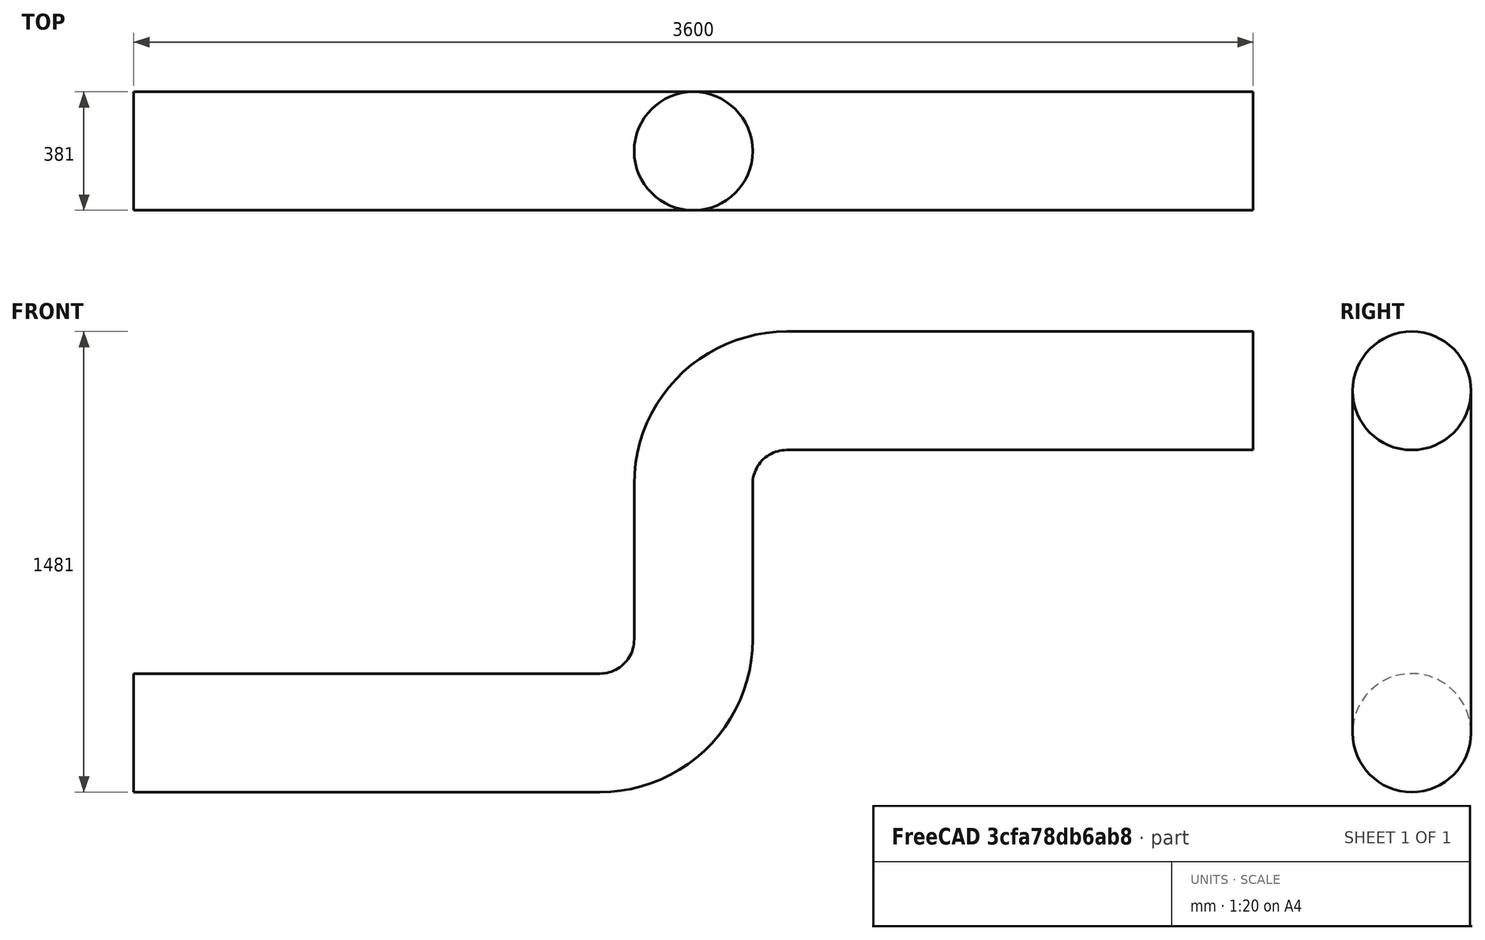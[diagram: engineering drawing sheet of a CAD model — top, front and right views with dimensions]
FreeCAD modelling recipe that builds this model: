
FCSTD DOCUMENT  (FreeCAD 0.21R33771 (Git))
Label: example_pipe
License: All rights reserved
LicenseURL: http://en.wikipedia.org/wiki/All_rights_reserved
objects: Part::FeaturePython×7, Sketcher::SketchObject×2, App::DocumentObjectGroupPython×2, PartDesign::AdditivePipe×1, PartDesign::Body×1, App::MaterialObjectPython×1, Fem::FemMeshObject×1
note: 12 computed .brp shape members not serialized (recipe doc carries the construction recipe); baked Part::Feature solids carry a one-line shape summary decoded from their .brp

FEATURE [Sketcher::SketchObject] Sketch
  FullyConstrained = true
  MapMode = 5
  Placement = pos=(0,0,0) rot=(0.57735,0.57735,0.57735;2.0944rad)
  Support = -> [YZ_Plane]
  sketch-geometry (1):
    g0: Circle CenterX=0 CenterY=0 CenterZ=0 NormalX=0 NormalY=0 NormalZ=1 AngleXU=0 Radius=190.5
  constraints (2):
    c: Coincident(g0,g-1)
    c: Diameter(g0) = 381
FEATURE [Sketcher::SketchObject] Sketch001
  FullyConstrained = false
  MapMode = 5
  Placement = pos=(0,0,0) rot=(1,0,0;1.5708rad)
  Support = -> [XZ_Plane]
  sketch-geometry (6):
    g0: LineSegment StartX=0 StartY=0 StartZ=0 EndX=1500 EndY=0 EndZ=0
    g1: LineSegment StartX=1800 StartY=300 StartZ=0 EndX=1800 EndY=800 EndZ=0
    g2: LineSegment StartX=2100 StartY=1100 StartZ=0 EndX=3600 EndY=1100 EndZ=0
    g3: ArcOfCircle CenterX=1500 CenterY=300 CenterZ=0 NormalX=0 NormalY=0 NormalZ=1 AngleXU=0 Radius=300 StartAngle=4.71239 EndAngle=6.28319
    g4: ArcOfCircle CenterX=1800 CenterY=800 CenterZ=0 NormalX=0 NormalY=0 NormalZ=1 AngleXU=0 Radius=1.41545e-06 StartAngle=1.5708 EndAngle=3.14159
    g5: ArcOfCircle CenterX=2100 CenterY=800 CenterZ=0 NormalX=0 NormalY=0 NormalZ=1 AngleXU=0 Radius=300 StartAngle=1.5708 EndAngle=3.14159
  constraints (13):
    c: Coincident(g-1,g0)
    c: Horizontal(g0)
    c: Vertical(g1)
    c: Horizontal(g2)
    c: Tangent(g0,g3) = -1.5708
    c: Tangent(g1,g3) = -1.5708
    c: DistanceX(g0,g0) = 1500
    c: Radius(g3) = 300
    c: Tangent(g1,g5) = 1.5708
    c: Tangent(g2,g5) = 1.5708
    c: Radius(g5) = 300
    c: DistanceY(g1,g1) = 500
    c: DistanceX(g2,g2) = 1500
FEATURE [PartDesign::AdditivePipe] AdditivePipe
  AuxilleryCurvelinear = true
  AuxillerySpineTangent = false
  Binormal = (0,0,0)
  Mode = 0
  Placement = pos=(0,0,0) rot=(0.57735,0.57735,0.57735;2.0944rad)
  Profile = -> Sketch
  Spine = -> Sketch001 [Edge1,Edge2,Edge3,Edge5,Edge6]
  SpineTangent = false
  Transformation = 0
  Transition = 0
FEATURE [PartDesign::Body] Body
  Group = -> [Sketch,Sketch001,AdditivePipe]
  Origin = -> Origin
  Tip = -> AdditivePipe
FEATURE [Part::FeaturePython] PhysicsModel  # WARN: FeaturePython — macro-defined, semantics opaque (R4)
  Flow = 0
  Phase = 0
  SRFModelAxis = (0,0,0)
  SRFModelCoR = (0,0,0)
  SRFModelEnabled = false
  SRFModelRPM = 0
  Time = 0
  Turbulence = 3
  TurbulenceModel = 0
  gx = 0
  gy = -9800
  gz = 0
FEATURE [App::MaterialObjectPython] FluidProperties  label="Water"  # material (typed FeaturePython)
  Category = 1
  Material = CardName=WaterIsothermal; Density=998 kg/m^3; Description=Standard distilled water properties at 20 Degrees Celsius and 1 atm; DynamicViscosity=1.003e-3 kg/m/s; Name=Water; Type=Isothermal
FEATURE [Part::FeaturePython] InitialiseFields  # WARN: FeaturePython — macro-defined, semantics opaque (R4)
  PotentialFlow = false
  PotentialFlowP = false
  Pressure = 0
  ReThetat = 1
  Temperature = 290
  UseInletTemperatureValue = false
  UseInletTurbulenceValues = false
  UseInletUValues = false
  UseOutletPValue = false
  Ux = 0
  Uy = 0
  Uz = 0
  epsilon = 50000000
  gammaInt = 1
  k = 860
  nuTilda = 55000000
  nut = 50000000
  omega = 2
FEATURE [Part::FeaturePython] CfdSolver  # WARN: FeaturePython — macro-defined, semantics opaque (R4)
  ConvergenceTol = 0.001
  EndTime = 1
  InputCaseName = case
  MaxCFLNumber = 5
  MaxInterfaceCFLNumber = 5
  MaxIterations = 2000
  Parallel = true
  ParallelCores = 4
  PurgeWrite = 0
  StartFrom = 0
  SteadyWriteInterval = 100
  TimeStep = 0.001
  TransientWriteInterval = 0.1
FEATURE [Part::FeaturePython] CfdFluidBoundary  label="inlet"  # WARN: FeaturePython — macro-defined, semantics opaque (R4)
  BoundarySubType = 5
  BoundaryType = 1
  DefaultBoundary = false
  DissipationRate = 50000000
  HeatFlux = 0
  HeatTransferCoeff = 0
  Intermittency = 1
  MassFlowRate = 0
  NuTilda = 55000000
  PeriodicCentreOfRotation = (0,0,0)
  PeriodicCentreOfRotationAxis = (0,0,0)
  PeriodicMaster = true
  PeriodicSeparationVector = (0,0,0)
  PorousBaffleMethod = 0
  Pressure = 100
  PressureDropCoeff = 0
  ReThetat = 1
  RelativeToFrame = false
  ReverseNormal = false
  RotationalPeriodic = false
  RoughnessConstant = 0.5
  RoughnessHeight = 0
  ScreenSpacing = 2
  ScreenWireDiameter = 0.2
  ShapeRefs = -> [AdditivePipe]
  SlipRatio = 0
  SpecificDissipationRate = 1
  Temperature = 290
  ThermalBoundaryType = 0
  TurbulenceInletSpecification = 0
  TurbulenceIntensityPercentage = 0.02
  TurbulenceLengthScale = 14
  TurbulentKineticEnergy = 10000
  TurbulentViscosity = 50000000
  Ux = 1000
  Uy = 0
  Uz = 0
  VelocityIsCartesian = true
  VelocityMag = 0
  VolFlowRate = 0
  kEqnTurbulentKineticEnergy = 10000
  kEqnTurbulentViscosity = 50000000
FEATURE [Part::FeaturePython] CfdFluidBoundary001  label="outlet"  # WARN: FeaturePython — macro-defined, semantics opaque (R4)
  BoundarySubType = 10
  BoundaryType = 2
  DefaultBoundary = false
  DissipationRate = 50000000
  HeatFlux = 0
  HeatTransferCoeff = 0
  Intermittency = 1
  MassFlowRate = 0
  NuTilda = 55000000
  PeriodicCentreOfRotation = (0,0,0)
  PeriodicCentreOfRotationAxis = (0,0,0)
  PeriodicMaster = true
  PeriodicSeparationVector = (0,0,0)
  PorousBaffleMethod = 0
  Pressure = 100
  PressureDropCoeff = 0
  ReThetat = 1
  RelativeToFrame = false
  ReverseNormal = false
  RotationalPeriodic = false
  RoughnessConstant = 0.5
  RoughnessHeight = 0
  ScreenSpacing = 2
  ScreenWireDiameter = 0.2
  ShapeRefs = -> [AdditivePipe]
  SlipRatio = 0
  SpecificDissipationRate = 1
  Temperature = 290
  ThermalBoundaryType = 0
  TurbulenceInletSpecification = 0
  TurbulenceIntensityPercentage = 1
  TurbulenceLengthScale = 100
  TurbulentKineticEnergy = 10000
  TurbulentViscosity = 50000000
  Ux = 0
  Uy = 0
  Uz = 0
  VelocityIsCartesian = true
  VelocityMag = 0
  VolFlowRate = 0
  kEqnTurbulentKineticEnergy = 10000
  kEqnTurbulentViscosity = 50000000
FEATURE [Part::FeaturePython] MeshRefinement  label="WallFaces"  # WARN: FeaturePython — macro-defined, semantics opaque (R4)
  ExpansionRatio = 1
  Extrusion = false
  ExtrusionAngle = 5
  ExtrusionAxisDirection = (1,0,0)
  ExtrusionAxisPoint = (0,0,0)
  ExtrusionLayers = 1
  ExtrusionRatio = 1
  ExtrusionThickness = 1
  ExtrusionType = 2DPlanar
  FirstLayerHeight = 0
  Internal = false
  KeepExistingMesh = false
  NumberLayers = 4
  RefinementThickness = 0
  RegionEdgeRefinement = 1
  RelativeLength = 0.75
  ShapeRefs = -> [AdditivePipe]
FEATURE [Part::FeaturePython] CfdFluidBoundary002  label="wall"  # WARN: FeaturePython — macro-defined, semantics opaque (R4)
  BoundarySubType = 0
  BoundaryType = 0
  DefaultBoundary = false
  DissipationRate = 50000000
  HeatFlux = 0
  HeatTransferCoeff = 0
  Intermittency = 1
  MassFlowRate = 0
  NuTilda = 55000000
  PeriodicCentreOfRotation = (0,0,0)
  PeriodicCentreOfRotationAxis = (0,0,0)
  PeriodicMaster = true
  PeriodicSeparationVector = (0,0,0)
  PorousBaffleMethod = 0
  Pressure = 100
  PressureDropCoeff = 0
  ReThetat = 1
  RelativeToFrame = false
  ReverseNormal = false
  RotationalPeriodic = false
  RoughnessConstant = 0.5
  RoughnessHeight = 0
  ScreenSpacing = 2
  ScreenWireDiameter = 0.2
  ShapeRefs = -> [AdditivePipe]
  SlipRatio = 0
  SpecificDissipationRate = 1
  Temperature = 290
  ThermalBoundaryType = 0
  TurbulenceInletSpecification = 0
  TurbulenceIntensityPercentage = 1
  TurbulenceLengthScale = 100
  TurbulentKineticEnergy = 10000
  TurbulentViscosity = 50000000
  Ux = 0
  Uy = 0
  Uz = 0
  VelocityIsCartesian = true
  VelocityMag = 0
  VolFlowRate = 0
  kEqnTurbulentKineticEnergy = 10000
  kEqnTurbulentViscosity = 50000000
FEATURE [Fem::FemMeshObject] AdditivePipe_MeshSurfaceMesh
FEATURE [App::DocumentObjectGroupPython] AdditivePipe_Mesh  # scripted group (container) (typed FeaturePython)
  CaseName = meshCase
  CellsBetweenLevels = 3
  CharacteristicLengthMax = 51
  ConvertToDualMesh = false
  EdgeRefinement = 1
  ElementDimension = 1
  Group = -> [MeshRefinement,AdditivePipe_MeshSurfaceMesh]
  ImplicitEdgeDetection = false
  MeshUtility = 0
  NumberOfProcesses = 1
  NumberOfThreads = 0
  Part = -> AdditivePipe
  PointInMesh = x=0 m; y=0 m; z=0 m
  STLAngularMeshDensity = 100
  STLRelativeLinearDeflection = 0.001
FEATURE [App::DocumentObjectGroupPython] CfdAnalysis  # scripted group (container) (typed FeaturePython)
  Group = -> [PhysicsModel,FluidProperties,InitialiseFields,CfdSolver,AdditivePipe_Mesh,CfdFluidBoundary,CfdFluidBoundary001,CfdFluidBoundary002]
  HostfileName = ../mpi_hostfile
  IsActiveAnalysis = true
  NeedsCaseRewrite = false
  NeedsMeshRerun = false
  NeedsMeshRewrite = false
  UseHostfile = false
